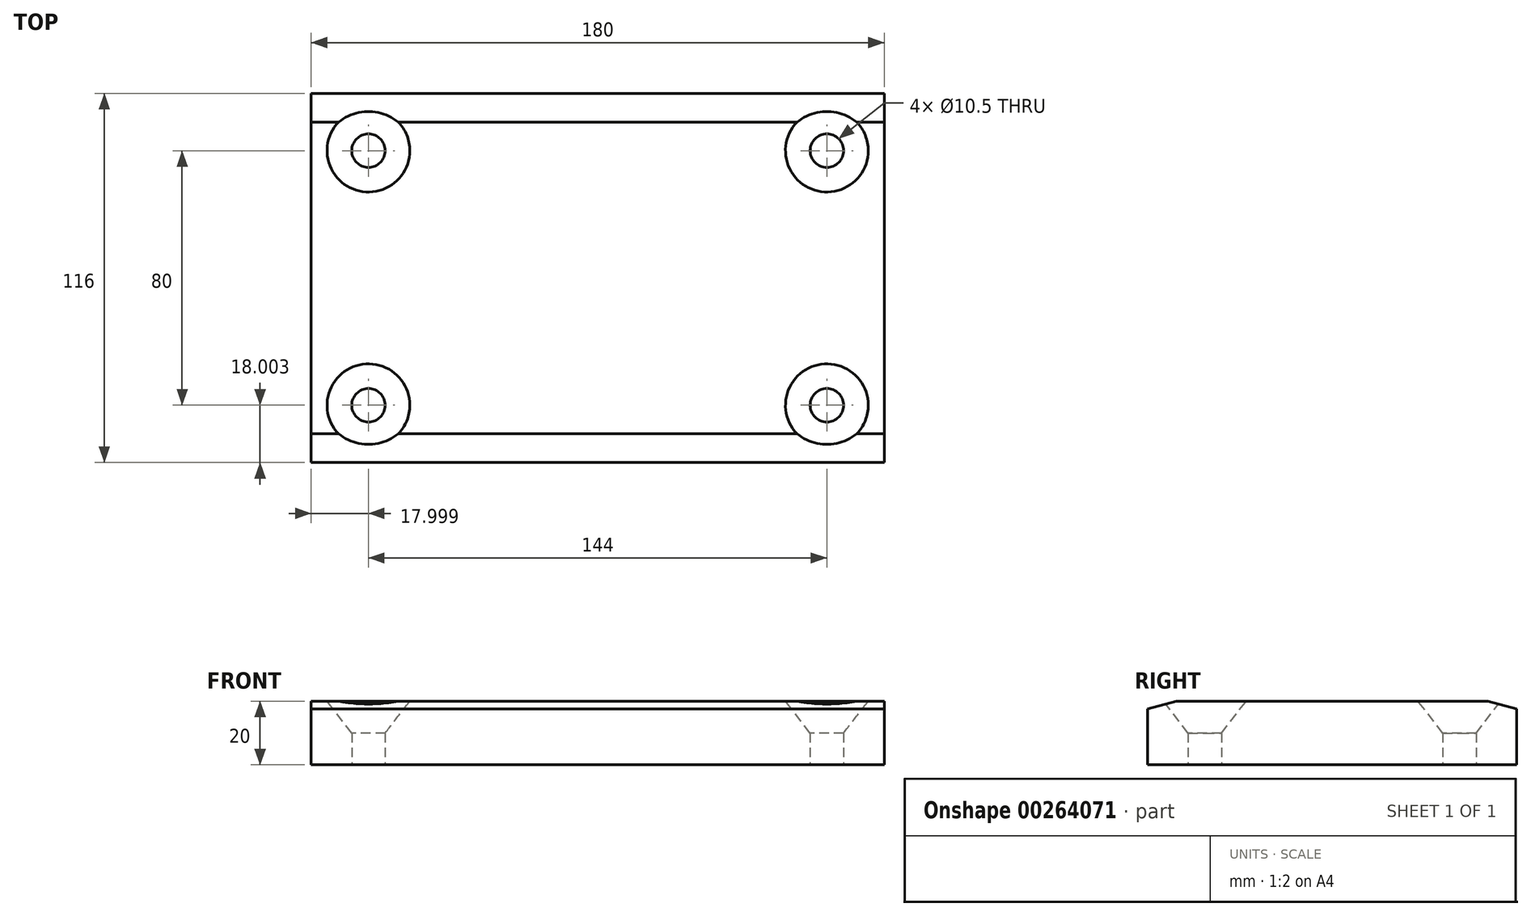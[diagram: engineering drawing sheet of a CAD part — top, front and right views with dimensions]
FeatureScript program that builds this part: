
annotation { "Feature Type Name" : "Feature", "Feature Type Description" : "" }
export const myFeature = defineFeature(function(context is Context, id is Id, definition is map)
    precondition{}
    {
        {
            var Q0;
            Q0=qCreatedBy(makeId("Top.planeOp"),FACE);
            var sketch = newSketch(context, id + "F0", { "sketchPlane" : qUnion([Q0])});
            skLineSegment(sketch, "E0.bottom", {"start": v(-96.86, 54.5) * mm, "end": v(83.14, 54.5) * mm});
            skLineSegment(sketch, "E0.top", {"start": v(-96.86, -61.5) * mm, "end": v(83.14, -61.5) * mm});
            skLineSegment(sketch, "E0.left", {"start": v(-96.86, 54.5) * mm, "end": v(-96.86, -61.5) * mm});
            skLineSegment(sketch, "E0.right", {"start": v(83.14, 54.5) * mm, "end": v(83.14, -61.5) * mm});
            skCircle(sketch, "E1", {"center": v(-78.86, 36.5) * mm, "radius": 5.25 * mm});
            skCircle(sketch, "E2", {"center": v(-78.86, -43.5) * mm, "radius": 5.25 * mm});
            skCircle(sketch, "E3", {"center": v(65.14, -43.5) * mm, "radius": 5.25 * mm});
            skCircle(sketch, "E4", {"center": v(65.14, 36.5) * mm, "radius": 5.25 * mm});
            skSolve(sketch);
        }
        {
            var Q0;
            Q0=makeQuery(id+"F0.imprint","IMPRINT",FACE,{"disambiguationData":[TD([[makeQuery(id+"F0.imprint","IMPRINT",EDGE,{"derivedFrom":sQuery(id+"F0.wireOp",EDGE,"E0.bottom")}),-1.0]])]});
            extrude(context, id + "F1", {"entities" : qUnion([Q0]), "depth" : 20 * mm});
        }
        {
            var Q0;
            Q0=makeQuery(id+"F1.opExtrude","CAP_EDGE",EDGE,{"disambiguationData":[OSD([sQuery(id+"F0.wireOp",EDGE,"E3")])],"isStart":false});
            var Q1;
            Q1=makeQuery(id+"F1.opExtrude","CAP_EDGE",EDGE,{"disambiguationData":[OSD([sQuery(id+"F0.wireOp",EDGE,"E2")])],"isStart":false});
            var Q2;
            Q2=makeQuery(id+"F1.opExtrude","CAP_EDGE",EDGE,{"disambiguationData":[OSD([sQuery(id+"F0.wireOp",EDGE,"E1")])],"isStart":false});
            var Q3;
            Q3=makeQuery(id+"F1.opExtrude","CAP_EDGE",EDGE,{"disambiguationData":[OSD([sQuery(id+"F0.wireOp",EDGE,"E4")])],"isStart":false});
            chamfer(context, id + "F2", {"entities" : qUnion([Q0, Q1, Q2, Q3]), "chamferType" : ChamferType.TWO_OFFSETS, "width1" : 10 * mm, "oppositeDirection" : false, "width2" : 7.75 * mm, "tangentPropagation" : true});
        }
        {
            var Q0;
            Q0=makeQuery(id+"F1.opExtrude","CAP_EDGE",EDGE,{"disambiguationData":[OSD([sQuery(id+"F0.wireOp",EDGE,"E0.top")])],"isStart":false});
            var Q1;
            Q1=makeQuery(id+"F1.opExtrude","CAP_EDGE",EDGE,{"disambiguationData":[OSD([sQuery(id+"F0.wireOp",EDGE,"E0.bottom")])],"isStart":false});
            chamfer(context, id + "F3", {"entities" : qUnion([Q0, Q1]), "chamferType" : ChamferType.OFFSET_ANGLE, "width" : 9 * mm, "oppositeDirection" : false, "angle" : 15 * degree, "tangentPropagation" : true});
        }
    });
